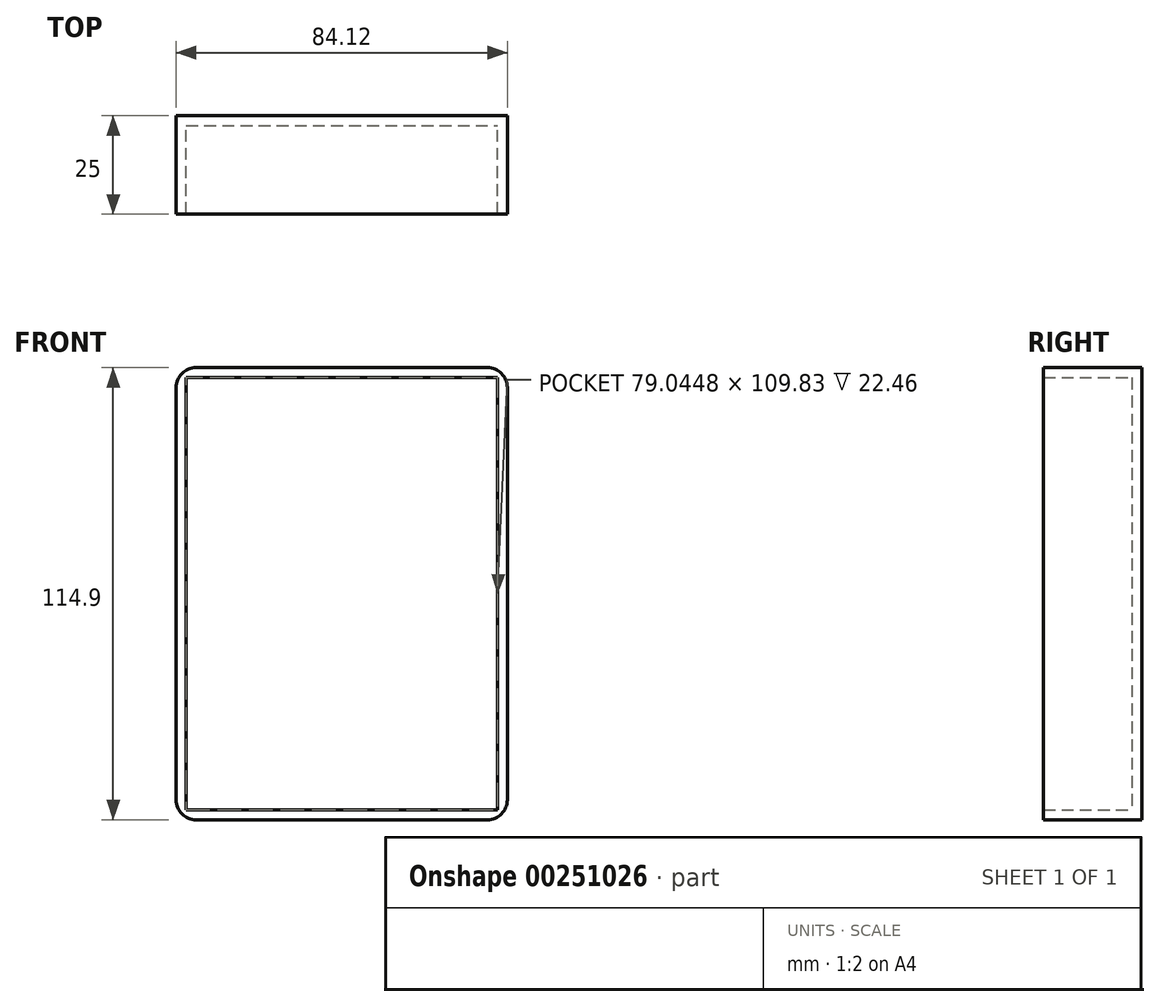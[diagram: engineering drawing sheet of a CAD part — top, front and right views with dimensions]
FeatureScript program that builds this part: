
annotation { "Feature Type Name" : "Feature", "Feature Type Description" : "" }
export const myFeature = defineFeature(function(context is Context, id is Id, definition is map)
    precondition{}
    {
        {
            var Q0;
            Q0=qCreatedBy(makeId("Front.planeOp"),FACE);
            var sketch = newSketch(context, id + "F0", { "sketchPlane" : qUnion([Q0])});
            skLineSegment(sketch, "E0.bottom", {"start": v(-42.06, 57.45) * mm, "end": v(42.06, 57.45) * mm});
            skLineSegment(sketch, "E0.top", {"start": v(-42.06, -57.45) * mm, "end": v(42.06, -57.45) * mm});
            skLineSegment(sketch, "E0.left", {"start": v(-42.06, 57.45) * mm, "end": v(-42.06, -57.45) * mm});
            skLineSegment(sketch, "E0.right", {"start": v(42.06, 57.45) * mm, "end": v(42.06, -57.45) * mm});
            skPoint(sketch, "E0.middle", {"position": v(0, 0) * mm});
            skSolve(sketch);
        }
        {
            var Q0;
            Q0=makeQuery(id+"F0.imprint","IMPRINT",FACE,{"disambiguationData":[TD([[makeQuery(id+"F0.imprint","IMPRINT",EDGE,{"derivedFrom":sQuery(id+"F0.wireOp",EDGE,"E0.bottom")}),-1.0]])]});
            extrude(context, id + "F1", {"entities" : qUnion([Q0]), "endBound" : BoundingType.SYMMETRIC, "depth" : 25 * mm});
        }
        {
            var Q0;
            Q0=makeQuery(id+"F1.opExtrude","CAP_FACE",FACE,{"disambiguationData":[OSD([sQuery(id+"F0.wireOp",EDGE,"E0.bottom"),sQuery(id+"F0.wireOp",EDGE,"E0.top"),sQuery(id+"F0.wireOp",EDGE,"E0.left"),sQuery(id+"F0.wireOp",EDGE,"E0.right")])],"isStart":false});
            shell(context, id + "F2", {"entities" : qUnion([Q0]), "thickness" : 2.54 * mm});
        }
        {
            var Q0;
            Q0=makeQuery(id+"F1.opExtrude","SWEPT_EDGE",EDGE,{"disambiguationData":[OSD([sQuery(id+"F0.wireOp",EDGE,"E0.bottom"),sQuery(id+"F0.wireOp",EDGE,"E0.left")])]});
            var Q1;
            Q1=makeQuery(id+"F1.opExtrude","SWEPT_EDGE",EDGE,{"disambiguationData":[OSD([sQuery(id+"F0.wireOp",EDGE,"E0.top"),sQuery(id+"F0.wireOp",EDGE,"E0.left")])]});
            var Q2;
            Q2=makeQuery(id+"F1.opExtrude","SWEPT_EDGE",EDGE,{"disambiguationData":[OSD([sQuery(id+"F0.wireOp",EDGE,"E0.bottom"),sQuery(id+"F0.wireOp",EDGE,"E0.right")])]});
            var Q3;
            Q3=makeQuery(id+"F1.opExtrude","SWEPT_EDGE",EDGE,{"disambiguationData":[OSD([sQuery(id+"F0.wireOp",EDGE,"E0.top"),sQuery(id+"F0.wireOp",EDGE,"E0.right")])]});
            fillet(context, id + "F3", {"entities" : qUnion([Q0, Q1, Q2, Q3]), "radius" : 5.08 * mm, "tangentPropagation" : true, "allowEdgeOverflow" : false});
        }
    });
